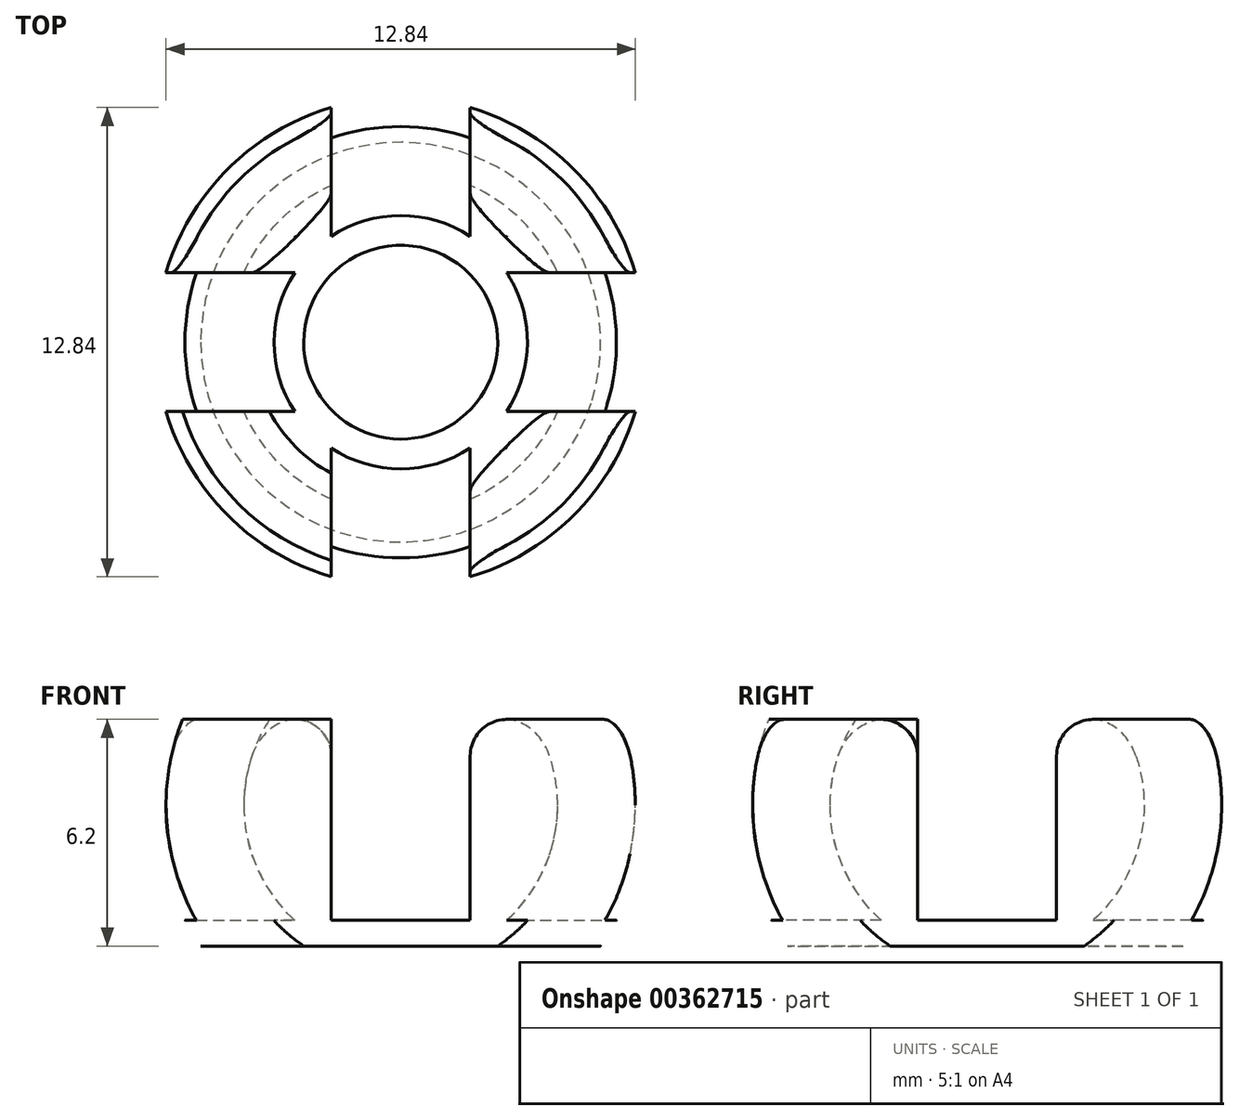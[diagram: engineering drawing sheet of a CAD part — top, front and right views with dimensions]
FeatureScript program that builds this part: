
annotation { "Feature Type Name" : "Feature", "Feature Type Description" : "" }
export const myFeature = defineFeature(function(context is Context, id is Id, definition is map)
    precondition{}
    {
        {
            var Q0;
            Q0=qCreatedBy(makeId("Front.planeOp"),FACE);
            var sketch = newSketch(context, id + "F0", { "sketchPlane" : qUnion([Q0])});
            skLineSegment(sketch, "E0", {"start": v(0, 11.3) * mm, "end": v(0, 9.55) * mm, "construction": true});
            skArc(sketch, "E1", {"start": v(0, 0) * mm, "mid": v(6.7, 6.65) * mm, "end": v(0, 13.3) * mm});
            skArc(sketch, "E2", {"start": v(0, 2) * mm, "mid": v(4.7, 6.65) * mm, "end": v(0, 11.3) * mm});
            skLineSegment(sketch, "E3", {"start": v(0, 13.3) * mm, "end": v(0, 11.3) * mm});
            skLineSegment(sketch, "E4", {"start": v(0, 2) * mm, "end": v(0, 0) * mm});
            skLineSegment(sketch, "E5.trimOffspring", {"start": v(0, 2) * mm, "end": v(0, -11.55) * mm, "construction": true});
            skSolve(sketch);
        }
        {
            var Q0;
            Q0=makeQuery(id+"F0.imprint","IMPRINT",FACE,{"disambiguationData":[TD([[makeQuery(id+"F0.imprint","IMPRINT",EDGE,{"derivedFrom":sQuery(id+"F0.wireOp",EDGE,"E1")}),1.0]])]});
            var Q1;
            Q1=sQuery(id+"F0.wireOp",EDGE,"E0");
            revolve(context, id + "F1", {"entities" : qUnion([Q0]), "axis" : qUnion([Q1]), "revolveType" : RevolveType.FULL});
        }
        {
            var Q0;
            Q0=qCreatedBy(makeId("Front.planeOp"),FACE);
            var sketch = newSketch(context, id + "F2", { "sketchPlane" : qUnion([Q0])});
            skLineSegment(sketch, "E6.bottom", {"start": v(-7.5, 9) * mm, "end": v(7.5, 9) * mm});
            skLineSegment(sketch, "E6.top", {"start": v(-7.5, 16) * mm, "end": v(7.5, 16) * mm});
            skLineSegment(sketch, "E6.left", {"start": v(-7.5, 9) * mm, "end": v(-7.5, 16) * mm});
            skLineSegment(sketch, "E6.right", {"start": v(7.5, 9) * mm, "end": v(7.5, 16) * mm});
            skSolve(sketch);
        }
        {
            var Q0;
            Q0=makeQuery(id+"F2.imprint","IMPRINT",FACE,{"disambiguationData":[TD([[makeQuery(id+"F2.imprint","IMPRINT",EDGE,{"derivedFrom":sQuery(id+"F2.wireOp",EDGE,"E6.bottom")}),1.0]])]});
            extrude(context, id + "F3", {"entities" : qUnion([Q0]), "operationType" : NewBodyOperationType.REMOVE, "endBound" : BoundingType.SYMMETRIC, "depth" : 25 * mm});
        }
        {
            var Q0;
            Q0=makeQuery(id+"F3.boolean.opBoolean","COPY",FACE,{"derivedFrom":makeQuery(id+"F3.opExtrude","SWEPT_FACE",FACE,{"disambiguationData":[OSD([sQuery(id+"F2.wireOp",EDGE,"E6.bottom")])]})});
            var sketch = newSketch(context, id + "F4", { "sketchPlane" : qUnion([Q0])});
            skLineSegment(sketch, "E7.bottom", {"start": v(-7, 1.9) * mm, "end": v(-1.9, 1.9) * mm});
            skLineSegment(sketch, "E7.top", {"start": v(-7, -1.9) * mm, "end": v(-1.9, -1.9) * mm});
            skLineSegment(sketch, "E7.left", {"start": v(-7, 1.9) * mm, "end": v(-7, -1.9) * mm});
            skLineSegment(sketch, "E7.right", {"start": v(7, 1.9) * mm, "end": v(7, -1.9) * mm});
            skLineSegment(sketch, "E8.bottom", {"start": v(-1.9, 7) * mm, "end": v(1.9, 7) * mm});
            skLineSegment(sketch, "E8.top", {"start": v(-1.9, -7) * mm, "end": v(1.9, -7) * mm});
            skLineSegment(sketch, "E8.left", {"start": v(-1.9, 7) * mm, "end": v(-1.9, 1.9) * mm});
            skLineSegment(sketch, "E8.right", {"start": v(1.9, 7) * mm, "end": v(1.9, 1.9) * mm});
            skLineSegment(sketch, "E9.trimOffspring", {"start": v(-1.9, -1.9) * mm, "end": v(-1.9, -7) * mm});
            skLineSegment(sketch, "E10.trimOffspring", {"start": v(1.9, 1.9) * mm, "end": v(7, 1.9) * mm});
            skLineSegment(sketch, "E11.trimOffspring", {"start": v(1.9, -1.9) * mm, "end": v(1.9, -7) * mm});
            skLineSegment(sketch, "E12.trimOffspring", {"start": v(1.9, -1.9) * mm, "end": v(7, -1.9) * mm});
            skSolve(sketch);
        }
        {
            var Q0;
            Q0 = qSketchRegion(id + "F4", true);
            extrude(context, id + "F5", {"entities" : qUnion([Q0]), "operationType" : NewBodyOperationType.REMOVE, "oppositeDirection" : true, "depth" : 5.5 * mm});
        }
        {
            var Q0;
            Q0=qCreatedBy(makeId("Front.planeOp"),FACE);
            var sketch = newSketch(context, id + "F6", { "sketchPlane" : qUnion([Q0])});
            skLineSegment(sketch, "E13.bottom", {"start": v(-7, 2.8) * mm, "end": v(7, 2.8) * mm});
            skLineSegment(sketch, "E13.top", {"start": v(-7, -1) * mm, "end": v(7, -1) * mm});
            skLineSegment(sketch, "E13.left", {"start": v(-7, 2.8) * mm, "end": v(-7, -1) * mm});
            skLineSegment(sketch, "E13.right", {"start": v(7, 2.8) * mm, "end": v(7, -1) * mm});
            skSolve(sketch);
        }
        {
            var Q0;
            Q0=makeQuery(id+"F6.imprint","IMPRINT",FACE,{"disambiguationData":[TD([[makeQuery(id+"F6.imprint","IMPRINT",EDGE,{"derivedFrom":sQuery(id+"F6.wireOp",EDGE,"E13.bottom")}),-1.0]])]});
            extrude(context, id + "F7", {"entities" : qUnion([Q0]), "operationType" : NewBodyOperationType.REMOVE, "endBound" : BoundingType.SYMMETRIC, "oppositeDirection" : true, "depth" : 25 * mm});
        }
        {
            var Q0;
            Q0=makeQuery(id+"F5.boolean.opBoolean","COPY",EDGE,{"derivedFrom":makeQuery(id+"F5.opExtrude","CAP_EDGE",EDGE,{"disambiguationData":[OSD([sQuery(id+"F4.wireOp",EDGE,"E10.trimOffspring")])],"isStart":true})});
            var Q1;
            Q1=makeQuery(id+"F5.boolean.opBoolean","COPY",EDGE,{"derivedFrom":makeQuery(id+"F5.opExtrude","CAP_EDGE",EDGE,{"disambiguationData":[OSD([sQuery(id+"F4.wireOp",EDGE,"E8.right")])],"isStart":true})});
            var Q2;
            Q2=makeQuery(id+"F5.boolean.opBoolean","COPY",EDGE,{"derivedFrom":makeQuery(id+"F5.opExtrude","CAP_EDGE",EDGE,{"disambiguationData":[OSD([sQuery(id+"F4.wireOp",EDGE,"E8.left")])],"isStart":true})});
            var Q3;
            Q3=makeQuery(id+"F5.boolean.opBoolean","COPY",EDGE,{"derivedFrom":makeQuery(id+"F5.opExtrude","CAP_EDGE",EDGE,{"disambiguationData":[OSD([sQuery(id+"F4.wireOp",EDGE,"E7.bottom")])],"isStart":true})});
            var Q4;
            Q4=makeQuery(id+"F5.boolean.opBoolean","COPY",EDGE,{"derivedFrom":makeQuery(id+"F5.opExtrude","CAP_EDGE",EDGE,{"disambiguationData":[OSD([sQuery(id+"F4.wireOp",EDGE,"E7.top")])],"isStart":true})});
            var Q5;
            Q5=makeQuery(id+"F5.boolean.opBoolean","COPY",EDGE,{"derivedFrom":makeQuery(id+"F5.opExtrude","CAP_EDGE",EDGE,{"disambiguationData":[OSD([sQuery(id+"F4.wireOp",EDGE,"E9.trimOffspring")])],"isStart":true})});
            var Q6;
            Q6=makeQuery(id+"F5.boolean.opBoolean","COPY",EDGE,{"derivedFrom":makeQuery(id+"F5.opExtrude","CAP_EDGE",EDGE,{"disambiguationData":[OSD([sQuery(id+"F4.wireOp",EDGE,"E11.trimOffspring")])],"isStart":true})});
            var Q7;
            Q7=makeQuery(id+"F5.boolean.opBoolean","COPY",EDGE,{"derivedFrom":makeQuery(id+"F5.opExtrude","CAP_EDGE",EDGE,{"disambiguationData":[OSD([sQuery(id+"F4.wireOp",EDGE,"E12.trimOffspring")])],"isStart":true})});
            fillet(context, id + "F8", {"entities" : qUnion([Q0, Q1, Q2, Q3, Q4, Q5, Q6, Q7]), "radius" : 1 * mm, "tangentPropagation" : true, "allowEdgeOverflow" : false});
        }
    });
